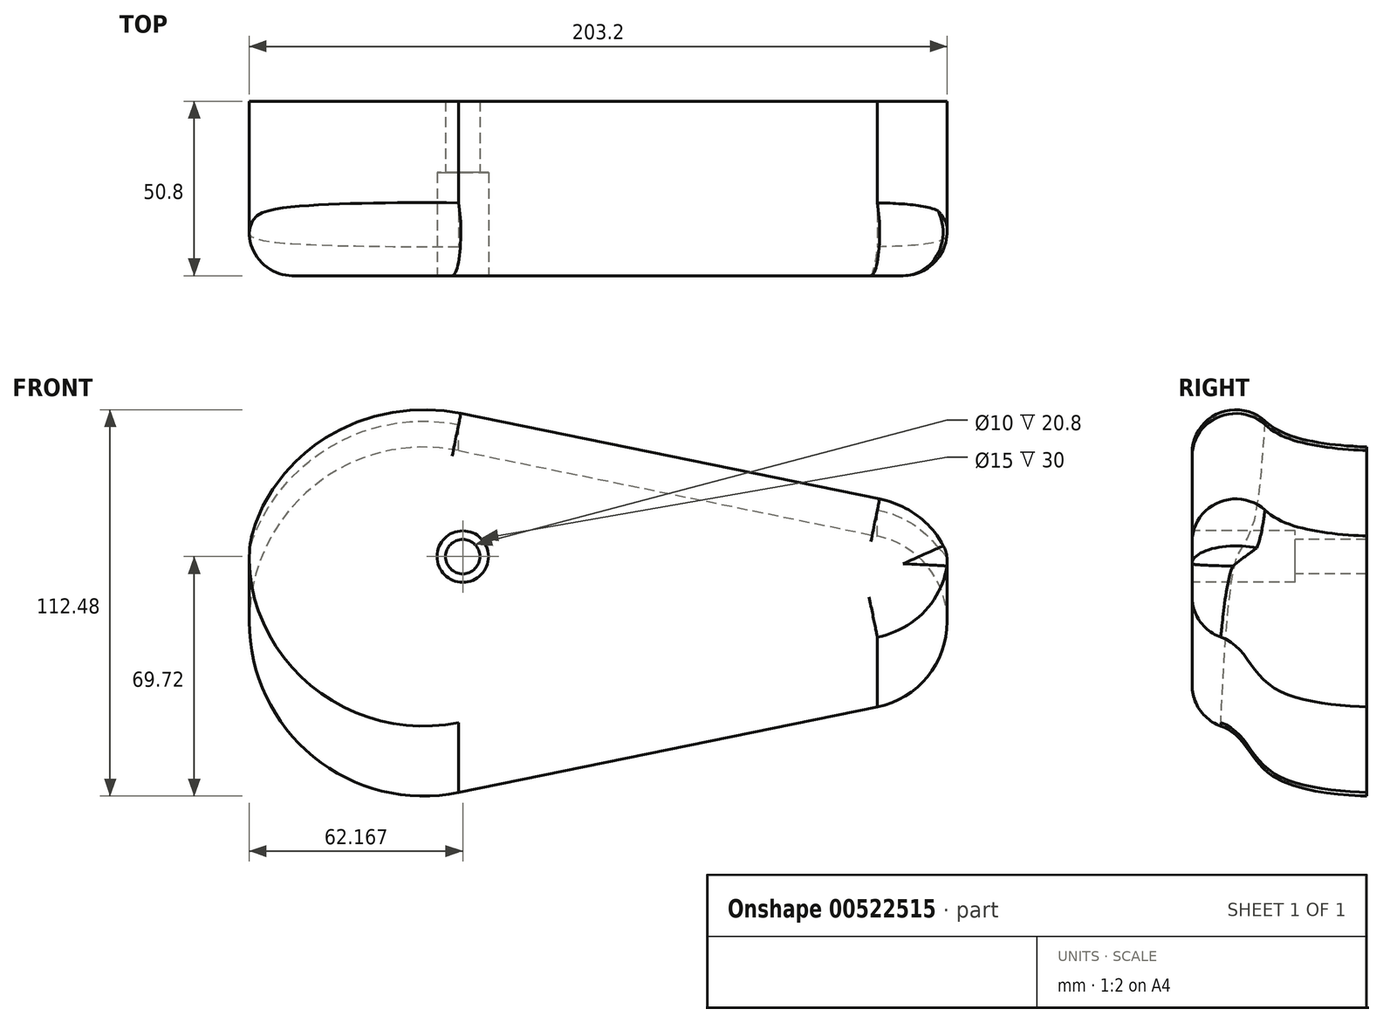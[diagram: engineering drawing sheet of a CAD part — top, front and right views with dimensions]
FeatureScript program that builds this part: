
annotation { "Feature Type Name" : "Feature", "Feature Type Description" : "" }
export const myFeature = defineFeature(function(context is Context, id is Id, definition is map)
    precondition{}
    {
        {
            var Q0;
            Q0=qCreatedBy(makeId("Front.planeOp"),FACE);
            var sketch = newSketch(context, id + "F0", { "sketchPlane" : qUnion([Q0])});
            skCircle(sketch, "E0", {"center": v(0, 0) * mm, "radius": 50.8 * mm});
            skCircle(sketch, "E1", {"center": v(127, 0) * mm, "radius": 25.4 * mm});
            skLineSegment(sketch, "E2", {"start": v(10.16, 49.77) * mm, "end": v(132.08, 24.89) * mm});
            skLineSegment(sketch, "E3", {"start": v(10.16, -49.77) * mm, "end": v(132.08, -24.89) * mm});
            skSolve(sketch);
        }
        {
            var Q0;
            Q0=qCreatedBy(makeId("Right.planeOp"),FACE);
            var sketch = newSketch(context, id + "F1", { "sketchPlane" : qUnion([Q0])});
            skFitSpline(sketch, "E4", {"points": [v(2.68, 0) * mm, v(-25.4, 6.35) * mm, v(-35.42, 17.84) * mm, v(-48.12, 21.6) * mm], "startDerivative": vector(-78.54, 3.89) * mm, "endDerivative": vector(-54.06, -0.45) * mm});
            skSolve(sketch);
        }
        {
            var Q0;
            Q0 = qSketchRegion(id + "F0", true);
            var Q1;
            Q1 = qConstructionFilter(qBodyType(qCreatedBy(id + "F1" ,EDGE), BodyType.WIRE), ConstructionObject.NO);
            sweep(context, id + "F2", {"profiles" : qUnion([Q0]), "path" : qUnion([Q1]), "keepProfileOrientation" : true});
        }
        {
            var Q0;
            Q0=makeQuery(id+"F2.opSweep","CAP_FACE",FACE,{"disambiguationData":[OSD([sQuery(id+"F0.wireOp",EDGE,"E0"),sQuery(id+"F0.wireOp",EDGE,"E1"),sQuery(id+"F0.wireOp",EDGE,"E2"),sQuery(id+"F0.wireOp",EDGE,"E3"),sQuery(id+"F1.wireOp",VERTEX,"E4.end")])],"isStart":false});
            fillet(context, id + "F3", {"entities" : qUnion([Q0]), "radius" : 12.7 * mm, "tangentPropagation" : true, "allowEdgeOverflow" : false});
        }
        {
            var Q0;
            Q0=makeQuery(id+"F2.opSweep","CAP_FACE",FACE,{"disambiguationData":[OSD([sQuery(id+"F0.wireOp",EDGE,"E0"),sQuery(id+"F0.wireOp",EDGE,"E1"),sQuery(id+"F0.wireOp",EDGE,"E2"),sQuery(id+"F0.wireOp",EDGE,"E3"),sQuery(id+"F1.wireOp",VERTEX,"E4.end")])],"isStart":false});
            var sketch = newSketch(context, id + "F4", { "sketchPlane" : qUnion([Q0])});
            skPoint(sketch, "E5", {"position": v(11.37, 18.77) * mm});
            skSolve(sketch);
        }
        {
            var Q0;
            Q0=sQuery(id+"F4.wireOp",VERTEX,"E5");
            var Q1;
            Q1=makeQuery(id+"F2.opSweep","SWEPT_BODY",BODY,{"disambiguationData":[OSD([sQuery(id+"F0.wireOp",EDGE,"E0"),sQuery(id+"F0.wireOp",EDGE,"E1"),sQuery(id+"F0.wireOp",EDGE,"E2"),sQuery(id+"F0.wireOp",EDGE,"E3"),sQuery(id+"F1.wireOp",EDGE,"E4")])]});
            hole(context, id + "F5", {"style" : HoleStyle.C_BORE, "endStyle" : HoleEndStyle.THROUGH, "holeDiameter" : 10 * mm, "cBoreDiameter" : 15 * mm, "cBoreDepth" : 30 * mm, "isTappedThrough" : true, "tappedDepth" : 12.7 * mm, "tapClearance" : 3, "startFromSketch" : true, "locations" : qUnion([Q0]), "scope" : qUnion([Q1])});
        }
    });
